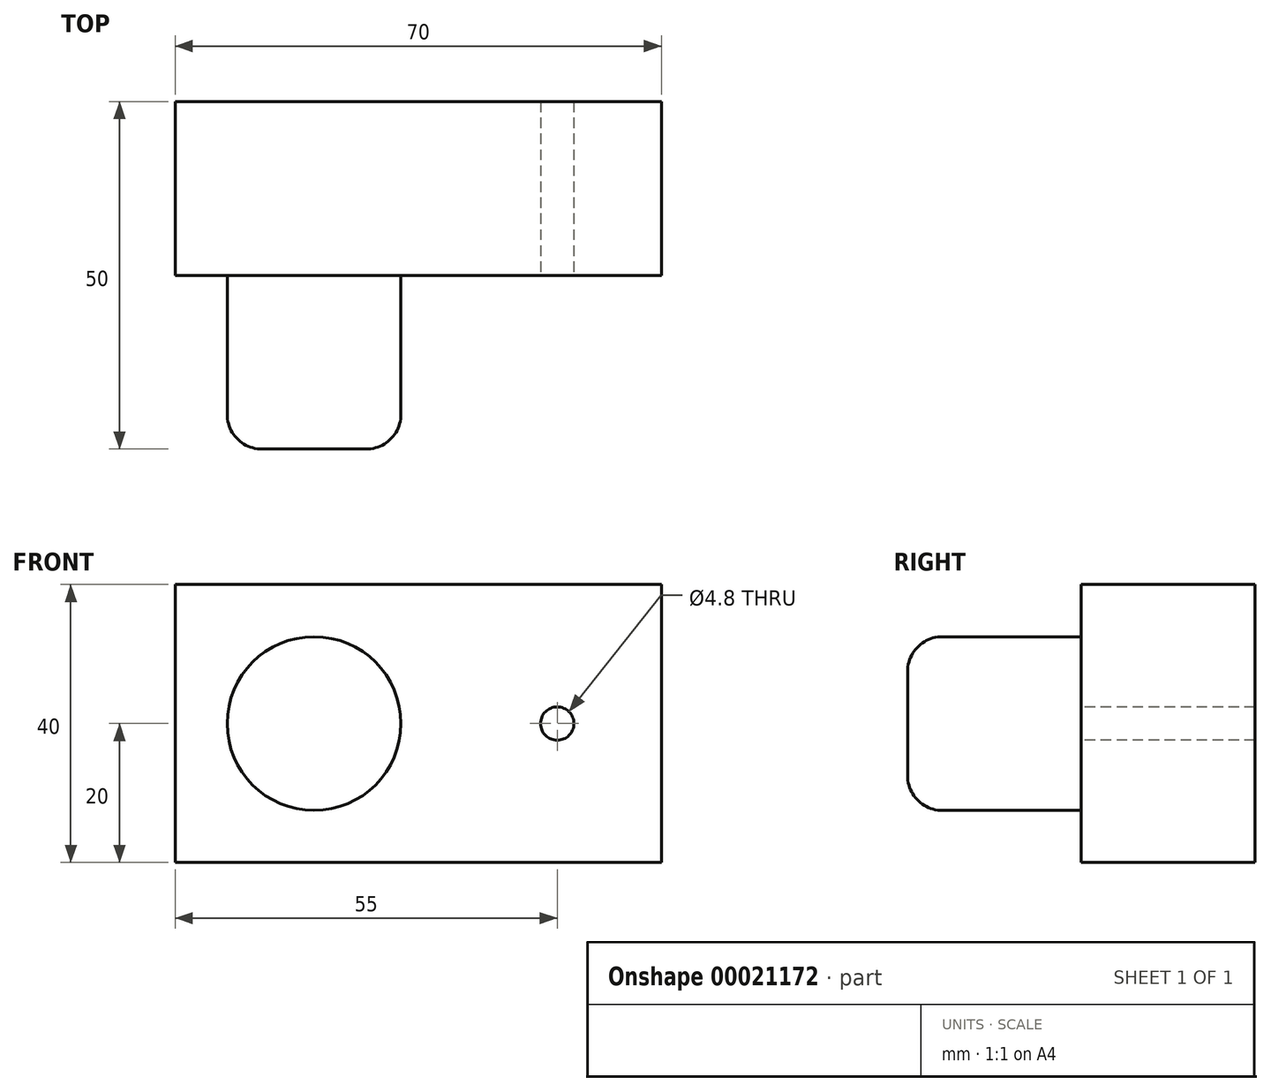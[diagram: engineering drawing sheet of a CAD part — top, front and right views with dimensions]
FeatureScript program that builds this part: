
annotation { "Feature Type Name" : "Feature", "Feature Type Description" : "" }
export const myFeature = defineFeature(function(context is Context, id is Id, definition is map)
    precondition{}
    {
        {
            var Q0;
            Q0=qCreatedBy(makeId("Front.planeOp"),FACE);
            var sketch = newSketch(context, id + "F0", { "sketchPlane" : qUnion([Q0])});
            skLineSegment(sketch, "E0.rect.bottom", {"start": v(35, 20) * mm, "end": v(-35, 20) * mm});
            skLineSegment(sketch, "E0.rect.top", {"start": v(35, -20) * mm, "end": v(-35, -20) * mm});
            skLineSegment(sketch, "E0.rect.left", {"start": v(35, 20) * mm, "end": v(35, -20) * mm});
            skLineSegment(sketch, "E0.rect.right", {"start": v(-35, 20) * mm, "end": v(-35, -20) * mm});
            skPoint(sketch, "E0.rect.middle", {"position": v(0, 0) * mm});
            skSolve(sketch);
        }
        {
            var Q0;
            Q0 = qSketchRegion(id + "F0", true);
            extrude(context, id + "F1", {"entities" : qUnion([Q0]), "endBound" : BoundingType.SYMMETRIC, "depth" : 25 * mm});
        }
        {
            var Q0;
            Q0=makeQuery(id+"F1.opExtrude","CAP_FACE",FACE,{"disambiguationData":[OSD([sQuery(id+"F0.wireOp",EDGE,"E0.rect.bottom"),sQuery(id+"F0.wireOp",EDGE,"E0.rect.top"),sQuery(id+"F0.wireOp",EDGE,"E0.rect.left"),sQuery(id+"F0.wireOp",EDGE,"E0.rect.right")])],"isStart":false});
            var sketch = newSketch(context, id + "F2", { "sketchPlane" : qUnion([Q0])});
            skCircle(sketch, "E1", {"center": v(-15, 0) * mm, "radius": 12.5 * mm});
            skSolve(sketch);
        }
        {
            var Q0;
            Q0 = qSketchRegion(id + "F2", true);
            extrude(context, id + "F3", {"entities" : qUnion([Q0]), "operationType" : NewBodyOperationType.ADD, "depth" : 25 * mm});
        }
        {
            var Q0;
            Q0=makeQuery(id+"F3.opExtrude","CAP_EDGE",EDGE,{"disambiguationData":[OSD([sQuery(id+"F2.wireOp",EDGE,"E1")])],"isStart":false});
            fillet(context, id + "F4", {"entities" : qUnion([Q0]), "radius" : 5 * mm, "tangentPropagation" : true, "allowEdgeOverflow" : false});
        }
        {
            var Q0;
            Q0=makeQuery(id+"F1.opExtrude","CAP_FACE",FACE,{"disambiguationData":[OSD([sQuery(id+"F0.wireOp",EDGE,"E0.rect.bottom"),sQuery(id+"F0.wireOp",EDGE,"E0.rect.top"),sQuery(id+"F0.wireOp",EDGE,"E0.rect.left"),sQuery(id+"F0.wireOp",EDGE,"E0.rect.right")])],"isStart":false});
            var sketch = newSketch(context, id + "F5", { "sketchPlane" : qUnion([Q0])});
            skPoint(sketch, "E2", {"position": v(20, 0) * mm});
            skSolve(sketch);
        }
        {
            var Q0;
            Q0=sQuery(id+"F5.wireOp",VERTEX,"E2");
            var Q1;
            Q1=makeQuery(id+"F1.opExtrude","SWEPT_BODY",BODY,{"disambiguationData":[OSD([sQuery(id+"F0.wireOp",EDGE,"E0.rect.bottom"),sQuery(id+"F0.wireOp",EDGE,"E0.rect.top"),sQuery(id+"F0.wireOp",EDGE,"E0.rect.left"),sQuery(id+"F0.wireOp",EDGE,"E0.rect.right")])]});
            hole(context, id + "F6", {"style" : HoleStyle.SIMPLE, "holeDiameter" : 4.8 * mm, "endStyle" : HoleEndStyle.THROUGH, "locations" : qUnion([Q0]), "scope" : qUnion([Q1])});
        }
    });
